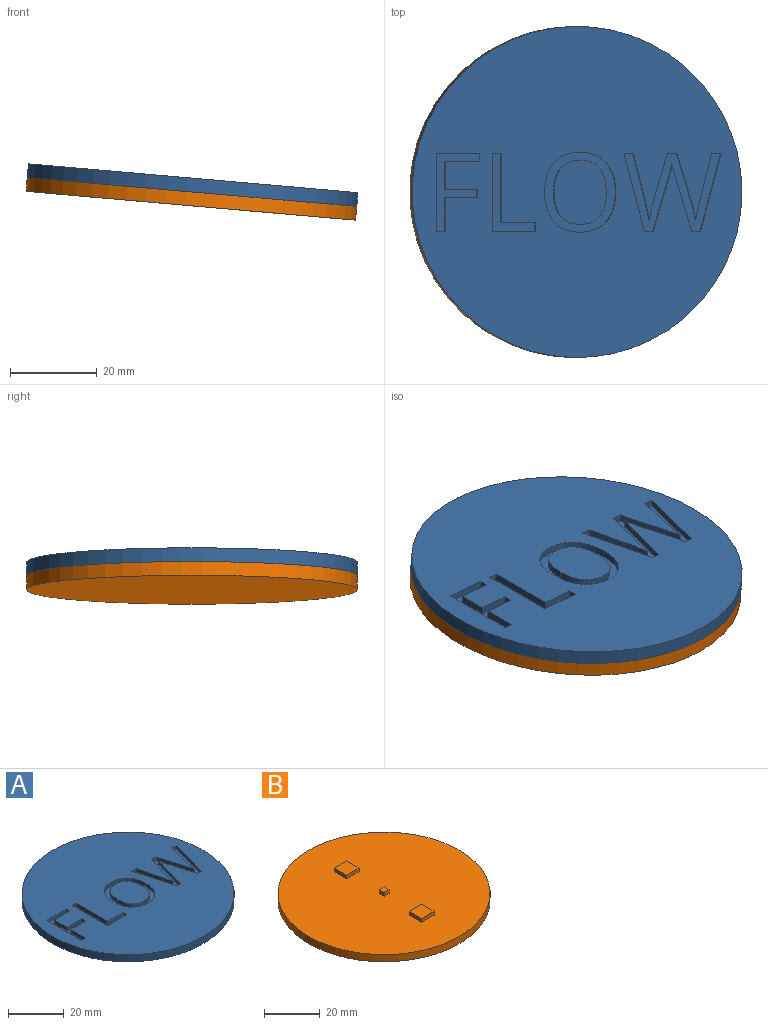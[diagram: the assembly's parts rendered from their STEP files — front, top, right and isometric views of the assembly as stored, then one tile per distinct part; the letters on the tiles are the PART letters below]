
ASSEMBLY  parts=2 mates=1
PART A: 75 faces, bbox 76.2x76.2x3.2 mm
  f0: plane 76.2x76.2mm, normal (0,0,-1), area 4457mm2, adj f2,f60,f61,f62,f63,f65,f66,f67
  f1: plane 76.2x76.2mm, normal (0,0,1), area 4059.1mm2, adj f2,f3,f4,f5,f6,f7,f8,f9
  f2: cylinder r=38.1mm len=76.2mm, axis (0,0,-1), area 760.1mm2, adj f0,f1
  f3: extruded ~6.75x2.16mm, area 11.5mm2, adj f1,f4,f18,f19
  f4: extruded ~6.01x2.44mm, area 10.6mm2, adj f1,f3,f5,f19
  f5: extruded ~6.11x2.4mm, area 10.8mm2, adj f1,f4,f6,f19
  f6: extruded ~6.77x2.15mm, area 11.5mm2, adj f1,f5,f7,f19
  f7: extruded ~6.81x2.15mm, area 11.6mm2, adj f1,f6,f8,f19
  f8: extruded ~6.09x2.41mm, area 10.7mm2, adj f1,f7,f9,f19
  f9: extruded ~6.03x2.46mm, area 10.7mm2, adj f1,f8,f18,f19
  f10: extruded ~5.46x1.59mm, area 9.2mm2, adj f11,f17,f19,f20
  f11: extruded ~4.51x1.88mm, area 8mm2, adj f10,f12,f19,f20
  f12: extruded ~4.47x1.86mm, area 8mm2, adj f11,f13,f19,f20
  f13: extruded ~5.47x1.59mm, area 9.2mm2, adj f12,f14,f19,f20
  f14: extruded ~5.51x1.59mm, area 9.3mm2, adj f13,f15,f19,f20
  f15: extruded ~4.48x1.87mm, area 8mm2, adj f14,f16,f19,f20
  f16: extruded ~4.49x1.88mm, area 8mm2, adj f15,f17,f19,f20
  f17: extruded ~5.51x1.59mm, area 9.3mm2, adj f10,f16,f19,f20
  f18: extruded ~6.75x2.17mm, area 11.5mm2, adj f1,f3,f9,f19
  f19: plane 18.4x16.44mm, normal (0,0,1), area 101mm2, adj f3,f4,f5,f6,f7,f8,f9,f10
  f20: plane 14.72x12.04mm, normal (0,0,1), area 146.8mm2, adj f10,f11,f12,f13,f14,f15,f16,f17
  f21: plane 9.96x1.59mm, normal (0,1,0), area 15.8mm2, adj f1,f22,f26,f27
  f22: plane 1.88x1.59mm, normal (-1,0,0), area 3mm2, adj f1,f21,f23,f27
  f23: plane 7.88x1.59mm, normal (0,-1,0), area 12.5mm2, adj f1,f22,f24,f27
  f24: plane 15.99x1.59mm, normal (-1,0,0), area 25.4mm2, adj f1,f23,f25,f27
  f25: plane 2.08x1.59mm, normal (0,-1,0), area 3.3mm2, adj f1,f24,f26,f27
  f26: plane 17.87x1.59mm, normal (1,0,0), area 28.4mm2, adj f1,f21,f25,f27
  f27: plane 17.87x9.96mm, normal (0,0,1), area 51.9mm2, adj f21,f22,f23,f24,f25,f26
  f28: plane 7.64x1.59mm, normal (-1,0,0), area 12.1mm2, adj f1,f29,f37,f38
  f29: plane 7.41x1.59mm, normal (0,1,0), area 11.8mm2, adj f1,f28,f30,f38
  f30: plane 1.85x1.59mm, normal (-1,0,0), area 2.9mm2, adj f1,f29,f31,f38
  f31: plane 7.41x1.59mm, normal (0,-1,0), area 11.8mm2, adj f1,f30,f32,f38
  f32: plane 6.54x1.59mm, normal (-1,0,0), area 10.4mm2, adj f1,f31,f33,f38
  f33: plane 7.88x1.59mm, normal (0,1,0), area 12.5mm2, adj f1,f32,f34,f38
  f34: plane 1.85x1.59mm, normal (-1,0,0), area 2.9mm2, adj f1,f33,f35,f38
  f35: plane 9.96x1.59mm, normal (0,-1,0), area 15.8mm2, adj f1,f34,f36,f38
  f36: plane 17.87x1.59mm, normal (1,0,0), area 28.4mm2, adj f1,f35,f37,f38
  f37: plane 2.08x1.59mm, normal (0,1,0), area 3.3mm2, adj f1,f28,f36,f38
  f38: plane 17.87x9.96mm, normal (0,0,1), area 65.3mm2, adj f28,f29,f30,f31,f32,f33,f34,f35
  f39: plane 17.87x4.78mm, normal (-0.97,0.26,0), area 29.4mm2, adj f1,f40,f58,f59
  f40: plane 2.2x1.59mm, normal (0,-1,0), area 3.5mm2, adj f1,f39,f41,f59
  f41: plane 11.01x2.81mm, normal (0.97,-0.25,0), area 18mm2, adj f1,f40,f42,f59
  f42: extruded ~4.23x1.59mm, area 6.9mm2, adj f1,f41,f43,f59
  f43: extruded ~4.28x1.59mm, area 7mm2, adj f1,f42,f44,f59
  f44: plane 10.96x3.36mm, normal (-0.96,-0.29,0), area 18.2mm2, adj f1,f43,f45,f59
  f45: plane 2.2x1.59mm, normal (0,-1,0), area 3.5mm2, adj f1,f44,f46,f59
  f46: plane 10.86x3.2mm, normal (0.96,-0.28,0), area 18mm2, adj f1,f45,f47,f59
  f47: extruded ~4.38x1.59mm, area 7.1mm2, adj f1,f46,f48,f59
  f48: extruded ~4.2x1.59mm, area 6.8mm2, adj f1,f47,f49,f59
  f49: plane 11.04x2.82mm, normal (-0.97,-0.25,0), area 18.1mm2, adj f1,f48,f50,f59
  f50: plane 2.2x1.59mm, normal (0,-1,0), area 3.5mm2, adj f1,f49,f51,f59
  f51: plane 17.87x4.76mm, normal (0.97,0.26,0), area 29.4mm2, adj f1,f50,f52,f59
  f52: plane 2.05x1.59mm, normal (0,1,0), area 3.3mm2, adj f1,f51,f53,f59
  f53: plane 11.89x3.5mm, normal (-0.96,0.28,0), area 19.7mm2, adj f1,f52,f54,f59
  f54: extruded ~3.53x1.59mm, area 5.8mm2, adj f1,f53,f55,f59
  f55: extruded ~1.59x1.45mm, area 2.4mm2, adj f1,f54,f56,f59
  f56: extruded ~2.01x1.59mm, area 3.3mm2, adj f1,f55,f57,f59
  f57: plane 11.96x3.61mm, normal (0.96,0.29,0), area 19.8mm2, adj f1,f56,f58,f59
  f58: plane 2.05x1.59mm, normal (0,1,0), area 3.3mm2, adj f1,f39,f57,f59
  f59: plane 22.5x17.87mm, normal (0,0,1), area 136.2mm2, adj f39,f40,f41,f42,f43,f44,f45,f46
  f60: plane 6.86x1.59mm, normal (0,-1,0), area 10.9mm2, adj f0,f61,f63,f64
  f61: plane 6.86x1.59mm, normal (-1,0,0), area 10.9mm2, adj f0,f60,f62,f64
  f62: plane 6.86x1.59mm, normal (0,1,0), area 10.9mm2, adj f0,f61,f63,f64
  f63: plane 6.86x1.59mm, normal (1,0,0), area 10.9mm2, adj f0,f60,f62,f64
  f64: plane 6.86x6.86mm, normal (0,0,-1), area 47mm2, adj f60,f61,f62,f63
  f65: plane 3.05x1.59mm, normal (1,0,0), area 4.8mm2, adj f0,f66,f68,f69
  f66: plane 3.05x1.59mm, normal (0,-1,0), area 4.8mm2, adj f0,f65,f67,f69
  f67: plane 3.05x1.59mm, normal (-1,0,0), area 4.8mm2, adj f0,f66,f68,f69
  f68: plane 3.05x1.59mm, normal (0,1,0), area 4.8mm2, adj f0,f65,f67,f69
  f69: plane 3.05x3.05mm, normal (0,0,-1), area 9.3mm2, adj f65,f66,f67,f68
  f70: plane 6.86x1.59mm, normal (-1,0,0), area 10.9mm2, adj f0,f71,f73,f74
  f71: plane 6.86x1.59mm, normal (0,1,0), area 10.9mm2, adj f0,f70,f72,f74
  f72: plane 6.86x1.59mm, normal (1,0,0), area 10.9mm2, adj f0,f71,f73,f74
  f73: plane 6.86x1.59mm, normal (0,-1,0), area 10.9mm2, adj f0,f70,f72,f74
  f74: plane 6.86x6.86mm, normal (0,0,-1), area 47mm2, adj f70,f71,f72,f73
PART B: 18 faces, bbox 76.2x76.2x4.8 mm
  f0: cylinder r=38.1mm len=76.2mm, axis (0,0,1), area 760.1mm2, adj f1,f2
  f1: plane 76.2x76.2mm, normal (0,0,-1), area 4560.4mm2, adj f0
  f2: plane 76.2x76.2mm, normal (0,0,1), area 4473.3mm2, adj f0,f3,f4,f5,f6,f8,f9,f10
  f3: plane 6.35x1.59mm, normal (0,1,0), area 10.1mm2, adj f2,f4,f6,f7
  f4: plane 6.35x1.59mm, normal (-1,0,0), area 10.1mm2, adj f2,f3,f5,f7
  f5: plane 6.35x1.59mm, normal (0,-1,0), area 10.1mm2, adj f2,f4,f6,f7
  f6: plane 6.35x1.59mm, normal (1,0,0), area 10.1mm2, adj f2,f3,f5,f7
  f7: plane 6.35x6.35mm, normal (0,0,1), area 40.3mm2, adj f3,f4,f5,f6
  f8: plane 2.54x1.59mm, normal (1,0,0), area 4mm2, adj f2,f9,f11,f12
  f9: plane 2.54x1.59mm, normal (0,1,0), area 4mm2, adj f2,f8,f10,f12
  f10: plane 2.54x1.59mm, normal (-1,0,0), area 4mm2, adj f2,f9,f11,f12
  f11: plane 2.54x1.59mm, normal (0,-1,0), area 4mm2, adj f2,f8,f10,f12
  f12: plane 2.54x2.54mm, normal (0,0,1), area 6.5mm2, adj f8,f9,f10,f11
  f13: plane 6.35x1.59mm, normal (1,0,0), area 10.1mm2, adj f2,f14,f16,f17
  f14: plane 6.35x1.59mm, normal (0,1,0), area 10.1mm2, adj f2,f13,f15,f17
  f15: plane 6.35x1.59mm, normal (-1,0,0), area 10.1mm2, adj f2,f14,f16,f17
  f16: plane 6.35x1.59mm, normal (0,-1,0), area 10.1mm2, adj f2,f13,f15,f17
  f17: plane 6.35x6.35mm, normal (0,0,1), area 40.3mm2, adj f13,f14,f15,f16
PLACE A rot(axis=(0,1,0),5deg) t=(-10.13,6.87,19.9)mm
PLACE B rot(axis=(0,1,0),5deg) t=(-10.13,6.87,19.9)mm
MATE fastened B.f0 <-> A.f2  axis (0.09,0,1) through (-9.99,6.87,21.48)mm
